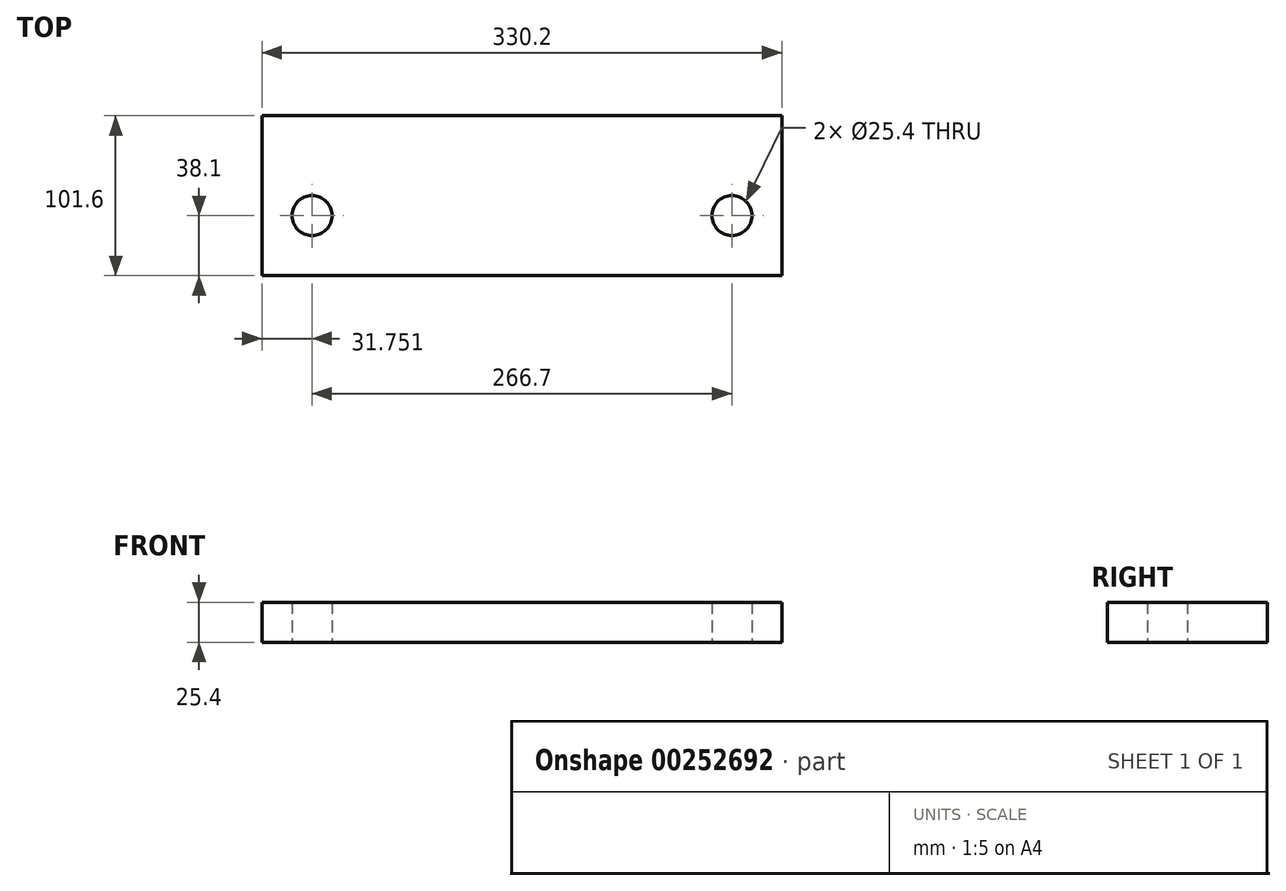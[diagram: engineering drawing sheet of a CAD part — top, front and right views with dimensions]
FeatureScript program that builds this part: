
annotation { "Feature Type Name" : "Feature", "Feature Type Description" : "" }
export const myFeature = defineFeature(function(context is Context, id is Id, definition is map)
    precondition{}
    {
        {
            var Q0;
            Q0=qCreatedBy(makeId("Top.planeOp"),FACE);
            var sketch = newSketch(context, id + "F0", { "sketchPlane" : qUnion([Q0])});
            skLineSegment(sketch, "E0.bottom", {"start": v(-89.54, 63.5) * mm, "end": v(75.56, 63.5) * mm});
            skLineSegment(sketch, "E0.top", {"start": v(-89.54, -38.1) * mm, "end": v(75.56, -38.1) * mm});
            skLineSegment(sketch, "E0.left", {"start": v(-89.54, 63.5) * mm, "end": v(-89.54, -38.1) * mm});
            skLineSegment(sketch, "E0.right", {"start": v(75.56, 63.5) * mm, "end": v(75.56, -38.1) * mm});
            skLineSegment(sketch, "E1", {"start": v(-89.54, 63.5) * mm, "end": v(-89.54, 0) * mm});
            skLineSegment(sketch, "E2", {"start": v(-89.54, -38.1) * mm, "end": v(-57.79, -38.1) * mm});
            skCircle(sketch, "E3", {"center": v(-57.79, 0) * mm, "radius": 12.7 * mm});
            skLineSegment(sketch, "E4.MirrorCS", {"start": v(240.66, 63.5) * mm, "end": v(75.56, 63.5) * mm});
            skLineSegment(sketch, "E5.MirrorCS", {"start": v(240.66, -38.1) * mm, "end": v(75.56, -38.1) * mm});
            skCircle(sketch, "E6.MirrorC", {"center": v(208.91, 0) * mm, "radius": 12.7 * mm});
            skLineSegment(sketch, "E7.MirrorCS", {"start": v(240.66, 63.5) * mm, "end": v(240.66, -38.1) * mm});
            skLineSegment(sketch, "E8.MirrorCS", {"start": v(240.66, 63.5) * mm, "end": v(240.66, 0) * mm});
            skLineSegment(sketch, "E9.MirrorCS", {"start": v(240.66, -38.1) * mm, "end": v(208.91, -38.1) * mm});
            skLineSegment(sketch, "E10", {"start": v(-89.54, 44.45) * mm, "end": v(240.66, 44.45) * mm});
            skSolve(sketch);
        }
        {
            var Q0;
            {var subQ0=sQuery(id+"F0.wireOp",EDGE,"E4.MirrorCS");Q0=makeQuery(id+"F0.imprint","IMPRINT",FACE,{"disambiguationData":[TD([[makeQuery(id+"F0.imprint","IMPRINT",EDGE,{"derivedFrom":subQ0}),1.0]])]});}
            var Q1;
            {var subQ5=sQuery(id+"F0.wireOp",EDGE,"E0.top");Q1=makeQuery(id+"F0.imprint","IMPRINT",FACE,{"disambiguationData":[TD([[makeQuery(id+"F0.imprint","IMPRINT",EDGE,{"derivedFrom":subQ5}),1.0]])]});}
            var Q2;
            {var subQ1=sQuery(id+"F0.wireOp",EDGE,"E5.MirrorCS");Q2=makeQuery(id+"F0.imprint","IMPRINT",FACE,{"disambiguationData":[TD([[makeQuery(id+"F0.imprint","IMPRINT",EDGE,{"derivedFrom":subQ1}),-1.0]])]});}
            var Q3;
            {var subQ0=sQuery(id+"F0.wireOp",EDGE,"E0.bottom");Q3=makeQuery(id+"F0.imprint","IMPRINT",FACE,{"disambiguationData":[TD([[makeQuery(id+"F0.imprint","IMPRINT",EDGE,{"derivedFrom":subQ0}),-1.0]])]});}
            extrude(context, id + "F1", {"entities" : qUnion([Q0, Q1, Q2, Q3]), "depth" : 25.4 * mm});
        }
    });
